# Revit family: Stirnplatte 45-40, VA
name_source: partatom
category: HLS-Bauteile
revit_build: Autodesk Revit 2017 (Build: 20190507_1515(x64)
units: mm (PartAtom-declared; Revit-internal decimal feet)

## family parameters
Basisbauteil = Fläche
Beim Laden mit Abzugskörper schneiden = Nein
Bemaßung runder Anschluss = Durchmesser verwenden
Gemeinsam genutzt = Ja
Raumberechnungspunkt = Nein
Teiletyp = Normal

## types (2) — shared parameters
Ausrichtung Platte = längs
Befestigung = Montageschiene
Breite Platte = 35 mm  [stored 0.114829 ft]
Fabrikat = MEFA
Firma = MEFA Befestigungs- und Montagesysteme GmbH
Gewicht = 0.36 kg
Gewicht pro Bauteil = 0.36 kg
Kurztext2 = für C-Profil 45
Lochabstand = 85 mm
Lochdurchmesser = 13 mm
Länge Platte = 115 mm  [stored 0.377297 ft]
Material = Edelstahl
Profil = C-Profil
Profilname = 45
Profiltyp = 45
Stärke Platte = 4 mm  [stored 0.0131234 ft]
Vorgabe-Ansicht = 1219 mm
max. Profilhöhe = 45 mm  [stored 0.147638 ft]
max. zul. Last Druck = 0.00 kip
zero-valued in all types: Länge, Sicherheitsfaktor

## per-type parameters (varying)
| type | 2-Lochplatte | Artikelnummer | EAN | Gewindeplatte 2-Loch | Kurztext1 | Sechskantschraube |
| Stirnplatte 45-40, V2A | MEFA 2-Lochplatte 60x 35x 4 VA : MEFA 2-Lochplatte 60x 35x 4 V2A | 0480656 | 4250928412799 | MEFA Gewindeplatte 2-Loch VA : MEFA Gewindeplatte 2-Loch V2A | Stirnplatte C-Profil 45 längs V2A | 6kt.Schraube DIN EN ISO 4017 VA : M12x 25 SW19 V2A |
| Stirnplatte 45-40, V4A | MEFA 2-Lochplatte 60x 35x 4 VA : MEFA 2-Lochplatte 60x 35x 4 V4A | 0481656 | 4250928413116 | MEFA Gewindeplatte 2-Loch VA : MEFA Gewindeplatte 2-Loch V4A | Stirnplatte C-Profil 45 längs V4A | 6kt.Schraube DIN EN ISO 4017 VA : M12x 25 SW19 V4A |

note: [stored X ft] marks values corroborated as IEEE doubles in the binary element streams (Revit-internal decimal feet)
